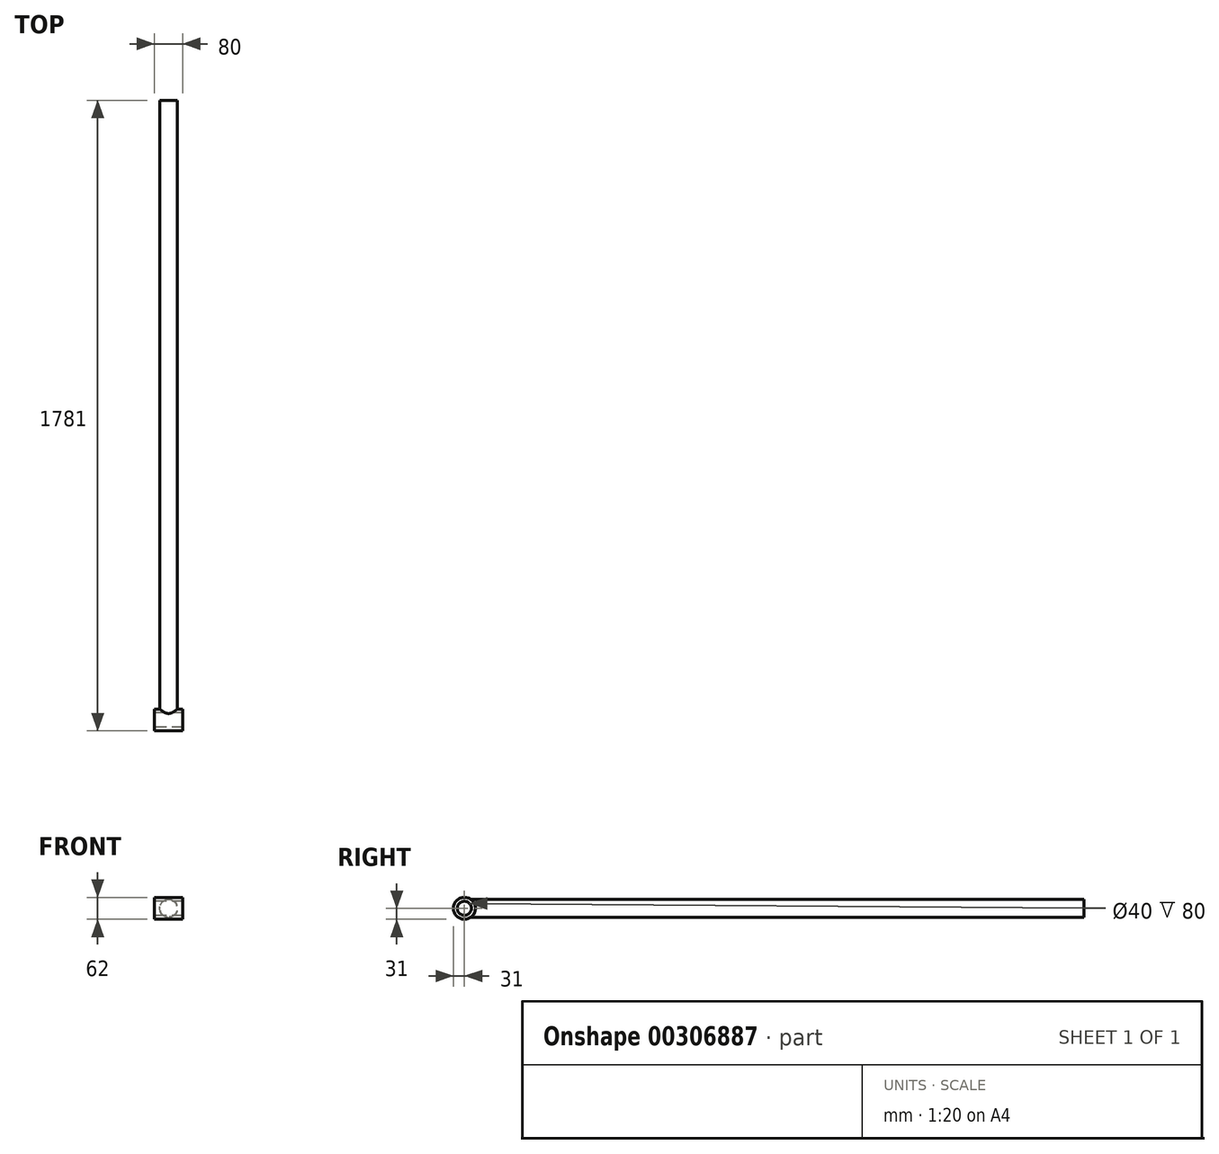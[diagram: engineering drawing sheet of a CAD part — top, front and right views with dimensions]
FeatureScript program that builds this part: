
annotation { "Feature Type Name" : "Feature", "Feature Type Description" : "" }
export const myFeature = defineFeature(function(context is Context, id is Id, definition is map)
    precondition{}
    {
        {
            var Q0;
            Q0=qCreatedBy(makeId("Right.planeOp"),FACE);
            cPlane(context, id + "F0", {"entities" : qUnion([Q0]), "cplaneType" : CPlaneType.OFFSET, "offset" : 40 * mm, "oppositeDirection" : true, "width" : 150 * mm, "height" : 150 * mm});
        }
        {
            var Q0;
            Q0=qCreatedBy(id+"F0.planeOp",FACE);
            var sketch = newSketch(context, id + "F1", { "sketchPlane" : qUnion([Q0])});
            skCircle(sketch, "E0", {"center": v(0, 0) * mm, "radius": 20 * mm});
            skCircle(sketch, "E1", {"center": v(0, 0) * mm, "radius": 31 * mm});
            skSolve(sketch);
        }
        {
            var Q0;
            Q0=qCreatedBy(makeId("Right.planeOp"),FACE);
            var sketch = newSketch(context, id + "F2", { "sketchPlane" : qUnion([Q0])});
            skCircle(sketch, "E2.0", {"center": v(0, 0) * mm, "radius": 31 * mm});
            skCircle(sketch, "E3.0", {"center": v(0, 0) * mm, "radius": 20 * mm});
            skSolve(sketch);
        }
        {
            var Q0;
            Q0 = qSketchRegion(id + "F2", true);
            extrude(context, id + "F3", {"entities" : qUnion([Q0]), "depth" : 80 * mm, "symmetric" : true});
        }
        {
            var Q0;
            Q0=qCreatedBy(makeId("Right.planeOp"),FACE);
            var sketch = newSketch(context, id + "F4", { "sketchPlane" : qUnion([Q0])});
            skPoint(sketch, "E4", {"position": v(1750, 0) * mm});
            skSolve(sketch);
        }
        {
            var Q0;
            Q0=qCreatedBy(makeId("Front.planeOp"),FACE);
            var Q1;
            Q1=sQuery(id+"F4.wireOp",VERTEX,"E4");
            cPlane(context, id + "F5", {"entities" : qUnion([Q0, Q1]), "cplaneType" : CPlaneType.PLANE_POINT, "offset" : 25 * mm, "width" : 150 * mm, "height" : 150 * mm});
        }
        {
            var Q0;
            Q0=qCreatedBy(id+"F5.planeOp",FACE);
            var sketch = newSketch(context, id + "F6", { "sketchPlane" : qUnion([Q0])});
            skCircle(sketch, "E5", {"center": v(0, 0) * mm, "radius": 25 * mm});
            skSolve(sketch);
        }
        {
            var Q0;
            Q0 = qSketchRegion(id + "F6", true);
            extrude(context, id + "F7", {"entities" : qUnion([Q0]), "operationType" : NewBodyOperationType.ADD, "endBound" : BoundingType.UP_TO_NEXT, "depth" : 25 * mm});
        }
    });
